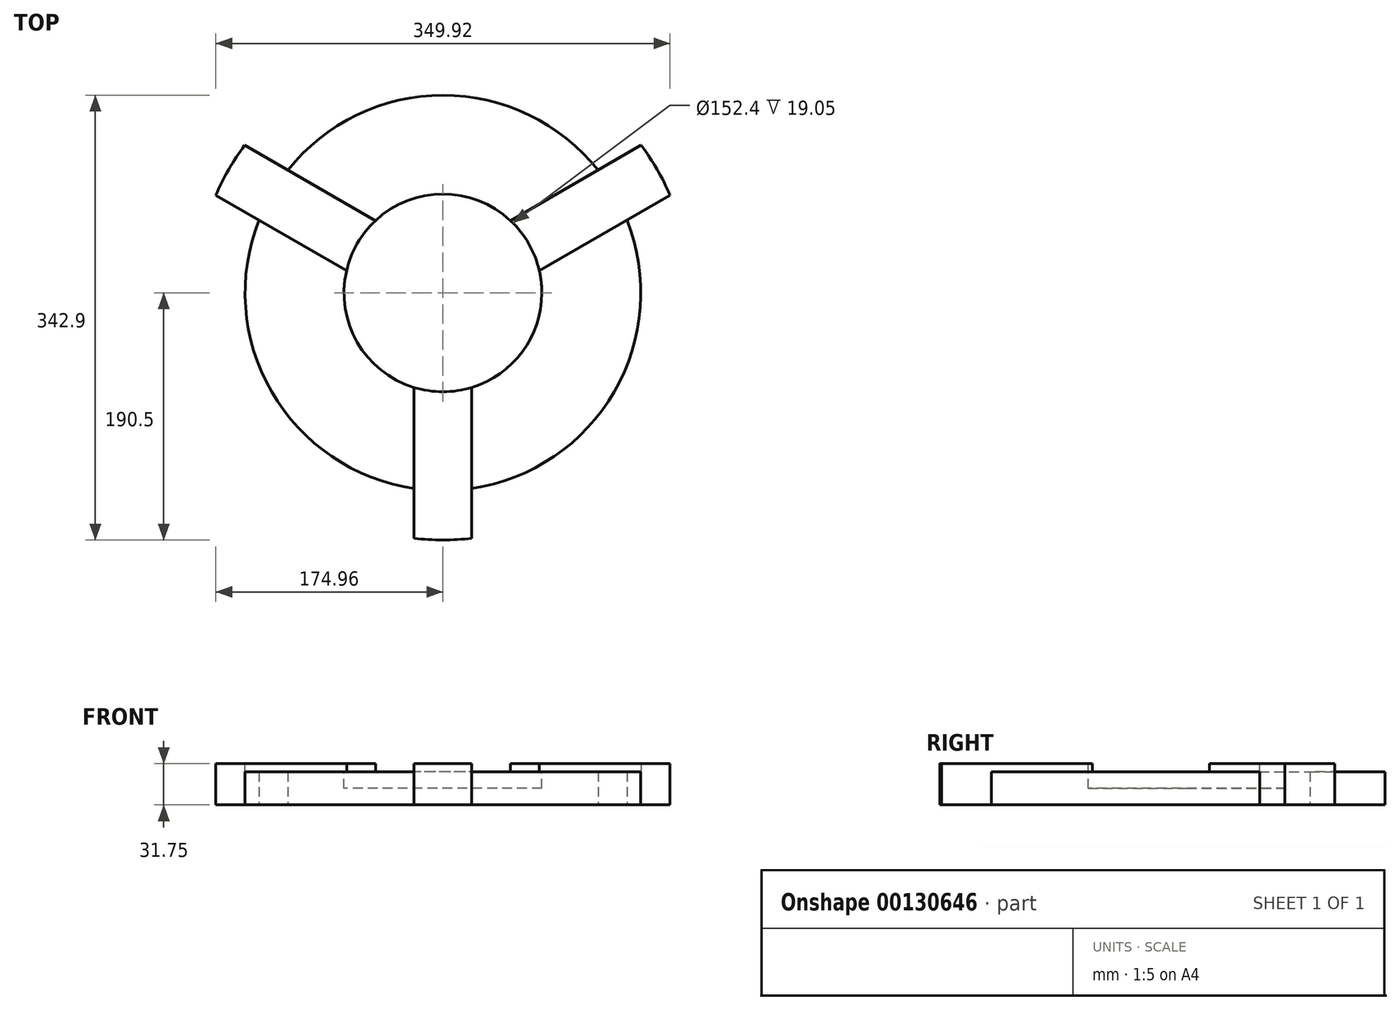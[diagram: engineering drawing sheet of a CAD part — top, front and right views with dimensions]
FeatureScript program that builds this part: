
annotation { "Feature Type Name" : "Feature", "Feature Type Description" : "" }
export const myFeature = defineFeature(function(context is Context, id is Id, definition is map)
    precondition{}
    {
        {
            var Q0;
            Q0=qCreatedBy(makeId("Top.planeOp"),FACE);
            var sketch = newSketch(context, id + "F0", { "sketchPlane" : qUnion([Q0])});
            skCircle(sketch, "E0", {"center": v(0, 0) * mm, "radius": 152.4 * mm});
            skLineSegment(sketch, "E1", {"start": v(0, 0) * mm, "end": v(0, -152.4) * mm, "construction": true});
            skLineSegment(sketch, "E2", {"start": v(0, 0) * mm, "end": v(-131.98, 76.2) * mm, "construction": true});
            skLineSegment(sketch, "E3", {"start": v(0, 0) * mm, "end": v(131.98, 76.2) * mm, "construction": true});
            skLineSegment(sketch, "E4", {"start": v(-22.23, -150.77) * mm, "end": v(22.23, -150.77) * mm, "construction": true});
            skLineSegment(sketch, "E5", {"start": v(141.68, 56.14) * mm, "end": v(119.46, 94.63) * mm, "construction": true});
            skLineSegment(sketch, "E6", {"start": v(-119.46, 94.63) * mm, "end": v(-141.68, 56.14) * mm, "construction": true});
            skPoint(sketch, "E7", {"position": v(0, -150.77) * mm});
            skPoint(sketch, "E8", {"position": v(-130.57, 75.39) * mm});
            skPoint(sketch, "E9", {"position": v(130.57, 75.39) * mm});
            skCircle(sketch, "E10", {"center": v(0, 0) * mm, "radius": 190.5 * mm});
            skLineSegment(sketch, "E11", {"start": v(-22.23, -150.77) * mm, "end": v(-22.23, -189.2) * mm});
            skLineSegment(sketch, "E12", {"start": v(22.23, -150.77) * mm, "end": v(22.23, -189.2) * mm});
            skLineSegment(sketch, "E13", {"start": v(141.68, 56.14) * mm, "end": v(174.96, 75.35) * mm});
            skLineSegment(sketch, "E14", {"start": v(119.46, 94.63) * mm, "end": v(152.74, 113.85) * mm});
            skLineSegment(sketch, "E15", {"start": v(-119.46, 94.63) * mm, "end": v(-152.74, 113.85) * mm});
            skLineSegment(sketch, "E16", {"start": v(-141.68, 56.14) * mm, "end": v(-174.96, 75.35) * mm});
            skLineSegment(sketch, "E17", {"start": v(0, 0) * mm, "end": v(-76.2, -131.98) * mm, "construction": true});
            skLineSegment(sketch, "E18", {"start": v(0, 0) * mm, "end": v(152.4, 0) * mm, "construction": true});
            skLineSegment(sketch, "E19", {"start": v(0, 0) * mm, "end": v(-76.2, 131.98) * mm, "construction": true});
            skLineSegment(sketch, "E20", {"start": v(-76.2, 131.98) * mm, "end": v(-95.25, 164.98) * mm});
            skLineSegment(sketch, "E21", {"start": v(152.4, 0) * mm, "end": v(190.5, 0) * mm});
            skLineSegment(sketch, "E22", {"start": v(-76.2, -131.98) * mm, "end": v(-95.25, -164.98) * mm});
            skSolve(sketch);
        }
        {
            var Q0;
            Q0=makeQuery(id+"F0.imprint","IMPRINT",FACE,{"disambiguationData":[TD([[makeQuery(id+"F0.imprint","IMPRINT",EDGE,{"derivedFrom":sQuery(id+"F0.wireOp",EDGE,"E0")}),1.0]])]});
            extrude(context, id + "F1", {"entities" : qUnion([Q0]), "depth" : 25.4 * mm});
        }
        {
            var Q0;
            Q0=makeQuery(id+"F1.opExtrude","CAP_FACE",FACE,{"disambiguationData":[OSD([sQuery(id+"F0.wireOp",EDGE,"E0")])],"isStart":false});
            var sketch = newSketch(context, id + "F2", { "sketchPlane" : qUnion([Q0])});
            skCircle(sketch, "E23", {"center": v(0, 0) * mm, "radius": 76.2 * mm});
            skLineSegment(sketch, "E24", {"start": v(-52, 55.7) * mm, "end": v(-119.46, 94.63) * mm});
            skLineSegment(sketch, "E25", {"start": v(-74.23, 17.2) * mm, "end": v(-141.68, 56.14) * mm});
            skLineSegment(sketch, "E26", {"start": v(-52, 55.7) * mm, "end": v(-74.23, 17.2) * mm, "construction": true});
            skLineSegment(sketch, "E27", {"start": v(74.23, 17.2) * mm, "end": v(141.68, 56.14) * mm});
            skLineSegment(sketch, "E28", {"start": v(52, 55.7) * mm, "end": v(119.46, 94.63) * mm});
            skLineSegment(sketch, "E29", {"start": v(74.23, 17.2) * mm, "end": v(52, 55.7) * mm, "construction": true});
            skLineSegment(sketch, "E30", {"start": v(-22.23, -72.89) * mm, "end": v(-22.23, -150.77) * mm});
            skLineSegment(sketch, "E31", {"start": v(22.23, -72.89) * mm, "end": v(22.23, -150.77) * mm});
            skLineSegment(sketch, "E32", {"start": v(-22.23, -72.89) * mm, "end": v(22.23, -72.89) * mm, "construction": true});
            skLineSegment(sketch, "E33", {"start": v(-63.12, 36.44) * mm, "end": v(0, 0) * mm, "construction": true});
            skLineSegment(sketch, "E34", {"start": v(0, -72.89) * mm, "end": v(0, 0) * mm, "construction": true});
            skLineSegment(sketch, "E35", {"start": v(63.12, 36.44) * mm, "end": v(0, 0) * mm, "construction": true});
            skLineSegment(sketch, "E36", {"start": v(0, 0) * mm, "end": v(76.2, -131.98) * mm, "construction": true});
            skLineSegment(sketch, "E37", {"start": v(0, 0) * mm, "end": v(131.98, -76.2) * mm, "construction": true});
            skLineSegment(sketch, "E38", {"start": v(0, 0) * mm, "end": v(-76.2, -131.98) * mm, "construction": true});
            skLineSegment(sketch, "E39", {"start": v(0, 0) * mm, "end": v(-131.98, -76.2) * mm, "construction": true});
            skLineSegment(sketch, "E40", {"start": v(0, 0) * mm, "end": v(-152.4, 0) * mm, "construction": true});
            skLineSegment(sketch, "E41", {"start": v(0, 0) * mm, "end": v(76.2, 131.98) * mm, "construction": true});
            skLineSegment(sketch, "E42", {"start": v(0, 0) * mm, "end": v(0, 152.4) * mm, "construction": true});
            skLineSegment(sketch, "E43", {"start": v(0, 0) * mm, "end": v(-76.2, 131.98) * mm, "construction": true});
            skLineSegment(sketch, "E44", {"start": v(0, 0) * mm, "end": v(152.4, 0) * mm, "construction": true});
            skPoint(sketch, "E45", {"position": v(-60.96, -105.59) * mm});
            skPoint(sketch, "E46", {"position": v(-45.72, -79.19) * mm});
            skPoint(sketch, "E47", {"position": v(-105.59, -60.96) * mm});
            skPoint(sketch, "E48", {"position": v(-79.19, -45.72) * mm});
            skPoint(sketch, "E49", {"position": v(-91.44, 0) * mm});
            skPoint(sketch, "E50", {"position": v(-121.92, 0) * mm});
            skSolve(sketch);
        }
        {
            var Q0;
            Q0=makeQuery(id+"F2.imprint","IMPRINT",FACE,{"disambiguationData":[TD([[makeQuery(id+"F2.imprint","IMPRINT",EDGE,{"derivedFrom":sQuery(id+"F2.wireOp",EDGE,"E23")}),1.0]])]});
            extrude(context, id + "F3", {"entities" : qUnion([Q0]), "operationType" : NewBodyOperationType.REMOVE, "oppositeDirection" : true, "depth" : 12.7 * mm});
        }
        {
            var Q0;
            {var subQ0=sQuery(id+"F2.wireOp",EDGE,"E24");Q0=makeQuery(id+"F2.imprint","IMPRINT",FACE,{"disambiguationData":[TD([[makeQuery(id+"F2.imprint","IMPRINT",EDGE,{"derivedFrom":subQ0}),1.0]])]});}
            var Q1;
            {var subQ0=sQuery(id+"F2.wireOp",EDGE,"E30");Q1=makeQuery(id+"F2.imprint","IMPRINT",FACE,{"disambiguationData":[TD([[makeQuery(id+"F2.imprint","IMPRINT",EDGE,{"derivedFrom":subQ0}),1.0]])]});}
            var Q2;
            {var subQ0=sQuery(id+"F2.wireOp",EDGE,"E27");Q2=makeQuery(id+"F2.imprint","IMPRINT",FACE,{"disambiguationData":[TD([[makeQuery(id+"F2.imprint","IMPRINT",EDGE,{"derivedFrom":subQ0}),1.0]])]});}
            extrude(context, id + "F4", {"entities" : qUnion([Q0, Q1, Q2]), "operationType" : NewBodyOperationType.ADD, "depth" : 6.35 * mm});
        }
        {
            var Q0;
            {var subQ0=sQuery(id+"F0.wireOp",EDGE,"E13");Q0=makeQuery(id+"F0.imprint","IMPRINT",FACE,{"disambiguationData":[TD([[makeQuery(id+"F0.imprint","IMPRINT",EDGE,{"derivedFrom":subQ0}),1.0]])]});}
            var Q1;
            {var subQ0=sQuery(id+"F0.wireOp",EDGE,"E15");Q1=makeQuery(id+"F0.imprint","IMPRINT",FACE,{"disambiguationData":[TD([[makeQuery(id+"F0.imprint","IMPRINT",EDGE,{"derivedFrom":subQ0}),1.0]])]});}
            var Q2;
            {var subQ0=sQuery(id+"F0.wireOp",EDGE,"E11");Q2=makeQuery(id+"F0.imprint","IMPRINT",FACE,{"disambiguationData":[TD([[makeQuery(id+"F0.imprint","IMPRINT",EDGE,{"derivedFrom":subQ0}),1.0]])]});}
            extrude(context, id + "F5", {"entities" : qUnion([Q0, Q1, Q2]), "operationType" : NewBodyOperationType.ADD, "depth" : 31.75 * mm});
        }
    });
